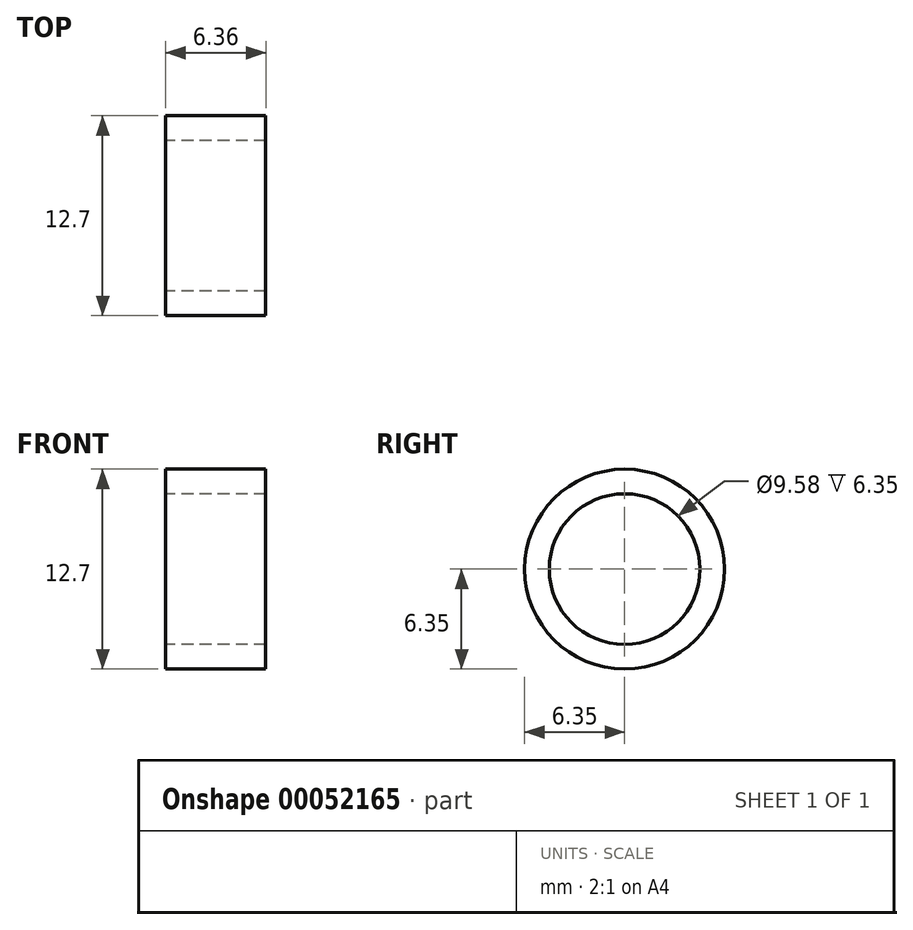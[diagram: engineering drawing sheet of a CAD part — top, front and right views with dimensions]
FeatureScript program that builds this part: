
annotation { "Feature Type Name" : "Feature", "Feature Type Description" : "" }
export const myFeature = defineFeature(function(context is Context, id is Id, definition is map)
    precondition{}
    {
        {
            var Q0;
            Q0=qCreatedBy(makeId("Right.planeOp"),FACE);
            var sketch = newSketch(context, id + "F0", { "sketchPlane" : qUnion([Q0])});
            skCircle(sketch, "E0", {"center": v(0, 0) * mm, "radius": 6.35 * mm});
            skCircle(sketch, "E1", {"center": v(0, 0) * mm, "radius": 4.79 * mm});
            skSolve(sketch);
        }
        {
            var Q0;
            Q0=makeQuery(id+"F0.imprint","IMPRINT",FACE,{"disambiguationData":[TD([[makeQuery(id+"F0.imprint","IMPRINT",EDGE,{"derivedFrom":sQuery(id+"F0.wireOp",EDGE,"E0")}),1.0]])]});
            extrude(context, id + "F1", {"entities" : qUnion([Q0]), "endBound" : BoundingType.SYMMETRIC, "depth" : 6.35 * mm});
        }
    });
